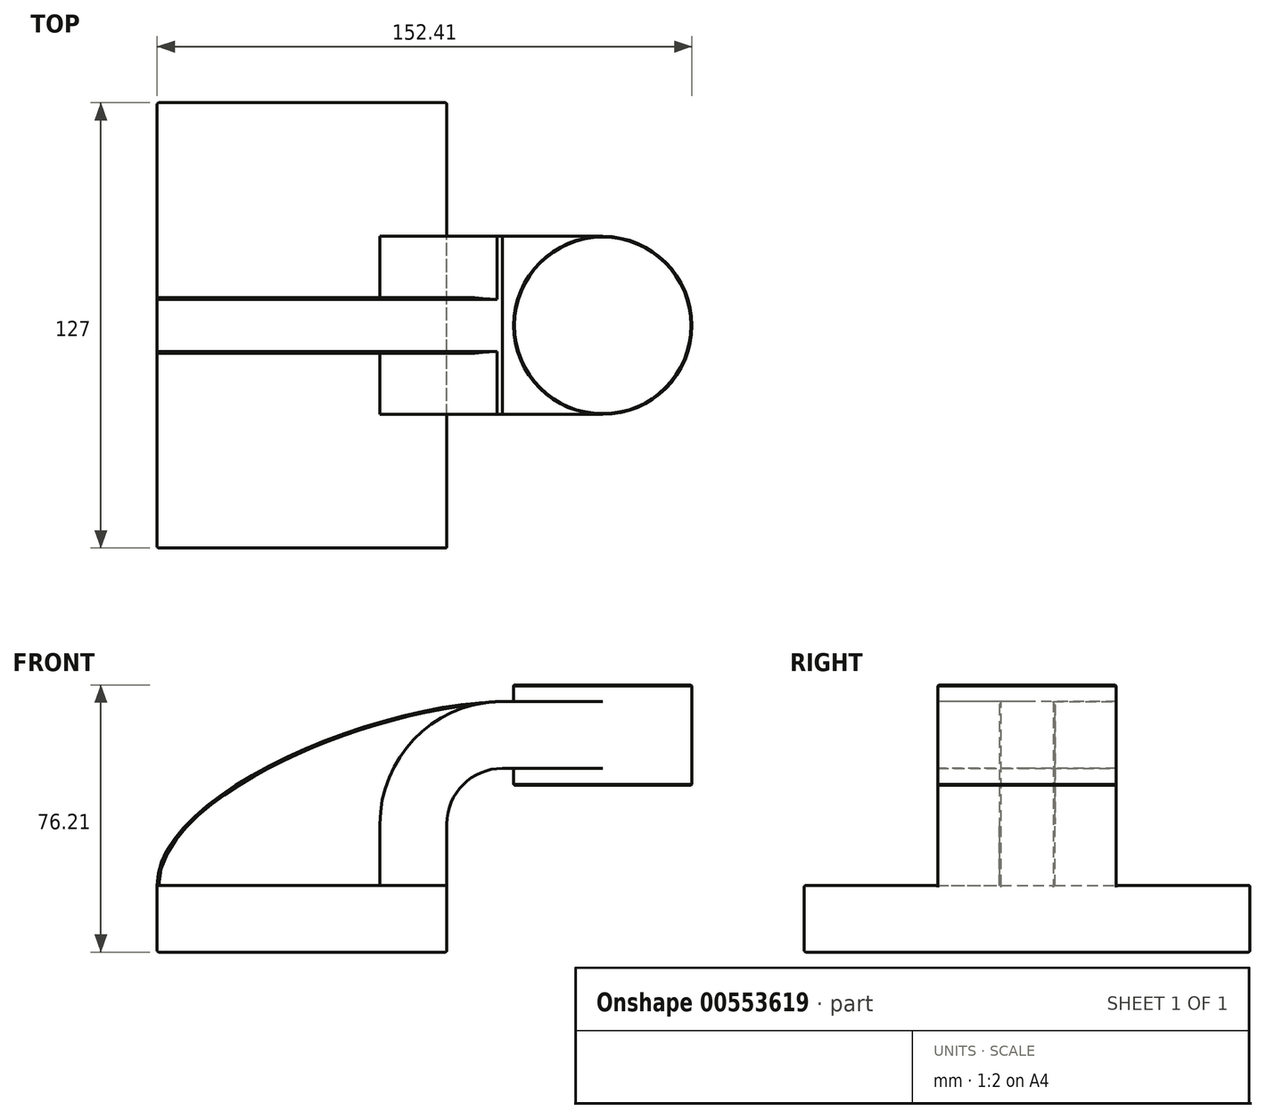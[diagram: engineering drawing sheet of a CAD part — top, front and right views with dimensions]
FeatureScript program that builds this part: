
annotation { "Feature Type Name" : "Feature", "Feature Type Description" : "" }
export const myFeature = defineFeature(function(context is Context, id is Id, definition is map)
    precondition{}
    {
        {
            var Q0;
            Q0=qCreatedBy(makeId("Front.planeOp"),FACE);
            var sketch = newSketch(context, id + "F0", { "sketchPlane" : qUnion([Q0])});
            skLineSegment(sketch, "E0.bottom", {"start": v(-41.27, -9.53) * mm, "end": v(41.28, -9.53) * mm});
            skLineSegment(sketch, "E0.top", {"start": v(-41.28, 9.52) * mm, "end": v(41.28, 9.52) * mm});
            skLineSegment(sketch, "E0.left", {"start": v(-41.28, -9.53) * mm, "end": v(-41.28, 9.52) * mm});
            skLineSegment(sketch, "E0.right", {"start": v(41.28, -9.53) * mm, "end": v(41.28, 9.52) * mm});
            skPoint(sketch, "E0.middle", {"position": v(0, 0) * mm});
            skLineSegment(sketch, "E1.bottom", {"start": v(60.33, 38.1) * mm, "end": v(111.13, 38.1) * mm});
            skLineSegment(sketch, "E1.top", {"start": v(60.33, 66.67) * mm, "end": v(111.13, 66.67) * mm});
            skLineSegment(sketch, "E1.left", {"start": v(60.33, 38.1) * mm, "end": v(60.32, 66.67) * mm});
            skLineSegment(sketch, "E1.right", {"start": v(111.13, 38.1) * mm, "end": v(111.13, 66.67) * mm});
            skPoint(sketch, "E1.middle", {"position": v(85.73, 52.39) * mm});
            skLineSegment(sketch, "E2", {"start": v(41.27, 9.52) * mm, "end": v(41.27, 27) * mm});
            skArc(sketch, "E3", {"start": v(41.27, 27) * mm, "mid": v(45.92, 38.23) * mm, "end": v(57.15, 42.88) * mm});
            skLineSegment(sketch, "E4", {"start": v(57.15, 42.88) * mm, "end": v(85.73, 42.88) * mm});
            skLineSegment(sketch, "E5.0", {"start": v(57.15, 61.93) * mm, "end": v(85.73, 61.93) * mm});
            skArc(sketch, "E5.1", {"start": v(22.22, 27) * mm, "mid": v(32.45, 51.7) * mm, "end": v(57.15, 61.93) * mm});
            skLineSegment(sketch, "E5.2", {"start": v(22.22, 9.52) * mm, "end": v(22.22, 27) * mm});
            skLineSegment(sketch, "E6", {"start": v(85.73, 38.1) * mm, "end": v(85.73, 66.67) * mm});
            skFitSpline(sketch, "E7", {"points": [v(-41.27, 9.53) * mm, v(57.15, 61.93) * mm], "startDerivative": vector(-0.82, 77.51) * mm, "endDerivative": vector(110.99, 1.46) * mm});
            skSolve(sketch);
        }
        {
            var Q0;
            Q0=makeQuery(id+"F0.imprint","IMPRINT",FACE,{"disambiguationData":[TD([[makeQuery(id+"F0.imprint","IMPRINT",EDGE,{"derivedFrom":sQuery(id+"F0.wireOp",EDGE,"E0.bottom")}),1.0]])]});
            extrude(context, id + "F1", {"entities" : qUnion([Q0]), "endBound" : BoundingType.SYMMETRIC, "depth" : 127 * mm, "offsetDistance" : 25.4 * mm});
        }
        {
            var Q0;
            {var subQ1=sQuery(id+"F0.wireOp",EDGE,"E2");Q0=makeQuery(id+"F0.imprint","IMPRINT",FACE,{"disambiguationData":[TD([[makeQuery(id+"F0.imprint","IMPRINT",EDGE,{"derivedFrom":subQ1}),1.0]])]});}
            var Q1;
            {var subQ0=sQuery(id+"F0.wireOp",EDGE,"E4");var subQ1=sQuery(id+"F0.wireOp",EDGE,"E1.left");var subQ2=makeQuery(id+"F0.imprint","INTERSECT",VERTEX,{"derivedFrom":[subQ1,subQ0]});Q1=makeQuery(id+"F0.imprint","IMPRINT",FACE,{"disambiguationData":[TD([[makeQuery(id+"F0.imprint","IMPRINT",EDGE,{"disambiguationData":[TD([[subQ2,-1.0]])],"derivedFrom":subQ1}),-1.0]])]});}
            extrude(context, id + "F2", {"entities" : qUnion([Q0, Q1]), "operationType" : NewBodyOperationType.ADD, "endBound" : BoundingType.SYMMETRIC, "depth" : 50.8 * mm, "offsetDistance" : 25.4 * mm});
        }
        {
            var Q0;
            {var subQ3=sQuery(id+"F0.wireOp",EDGE,"E5.2");Q0=makeQuery(id+"F0.imprint","IMPRINT",FACE,{"disambiguationData":[TD([[makeQuery(id+"F0.imprint","IMPRINT",EDGE,{"derivedFrom":subQ3}),1.0]])]});}
            extrude(context, id + "F3", {"entities" : qUnion([Q0]), "operationType" : NewBodyOperationType.ADD, "endBound" : BoundingType.SYMMETRIC, "depth" : 15.88 * mm, "offsetDistance" : 25.4 * mm});
        }
        {
            var Q0;
            {var subQ4=sQuery(id+"F0.wireOp",EDGE,"E1.right");Q0=makeQuery(id+"F0.imprint","IMPRINT",FACE,{"disambiguationData":[TD([[makeQuery(id+"F0.imprint","IMPRINT",EDGE,{"derivedFrom":subQ4}),1.0]])]});}
            var Q1;
            Q1=sQuery(id+"F0.wireOp",EDGE,"E6");
            revolve(context, id + "F4", {"operationType" : NewBodyOperationType.ADD, "entities" : qUnion([Q0]), "axis" : qUnion([Q1]), "revolveType" : RevolveType.FULL});
        }
        {
            var Q0;
            Q0=makeQuery(id+"F1.opExtrude","CAP_EDGE",EDGE,{"disambiguationData":[OSD([sQuery(id+"F0.wireOp",EDGE,"E0.left")])],"isStart":false});
            var Q1;
            Q1=makeQuery(id+"F1.opExtrude","CAP_EDGE",EDGE,{"disambiguationData":[OSD([sQuery(id+"F0.wireOp",EDGE,"E0.right")])],"isStart":false});
            var Q2;
            Q2=makeQuery(id+"F1.opExtrude","CAP_EDGE",EDGE,{"disambiguationData":[OSD([sQuery(id+"F0.wireOp",EDGE,"E0.top")])],"isStart":false});
            var Q3;
            {var subQ0=sQuery(id+"F0.wireOp",EDGE,"E7");var subQ1=sQuery(id+"F0.wireOp",EDGE,"E0.top");var subQ2=sQuery(id+"F0.wireOp",EDGE,"E0.left");Q3=makeQuery(id+"F3.boolean.opBoolean","SPLIT",EDGE,{"disambiguationData":[TD([makeQuery(id+"F1.opExtrude","CAP_FACE",FACE,{"disambiguationData":[OSD([sQuery(id+"F0.wireOp",EDGE,"E0.bottom"),subQ1,subQ2,sQuery(id+"F0.wireOp",EDGE,"E0.right")])],"isStart":false})])],"derivedFrom":makeQuery(id+"F1.opExtrude","SWEPT_EDGE",EDGE,{"disambiguationData":[OSD([subQ1,subQ2,subQ0])]})});}
            var Q4;
            {var subQ0=sQuery(id+"F0.wireOp",EDGE,"E0.left");var subQ1=sQuery(id+"F0.wireOp",EDGE,"E0.top");var subQ2=sQuery(id+"F0.wireOp",EDGE,"E7");Q4=makeQuery(id+"F3.boolean.opBoolean","SPLIT",EDGE,{"disambiguationData":[TD([makeQuery(id+"F1.opExtrude","CAP_FACE",FACE,{"disambiguationData":[OSD([sQuery(id+"F0.wireOp",EDGE,"E0.bottom"),subQ1,subQ0,sQuery(id+"F0.wireOp",EDGE,"E0.right")])],"isStart":true})])],"derivedFrom":makeQuery(id+"F1.opExtrude","SWEPT_EDGE",EDGE,{"disambiguationData":[OSD([subQ1,subQ0,subQ2])]})});}
            var Q5;
            Q5=makeQuery(id+"F1.opExtrude","CAP_EDGE",EDGE,{"disambiguationData":[OSD([sQuery(id+"F0.wireOp",EDGE,"E0.top")])],"isStart":true});
            var Q6;
            {var subQ0=sQuery(id+"F0.wireOp",EDGE,"E2");var subQ1=sQuery(id+"F0.wireOp",EDGE,"E0.top");var subQ2=sQuery(id+"F0.wireOp",EDGE,"E0.right");Q6=makeQuery(id+"F2.boolean.opBoolean","SPLIT",EDGE,{"disambiguationData":[TD([makeQuery(id+"F1.opExtrude","CAP_FACE",FACE,{"disambiguationData":[OSD([sQuery(id+"F0.wireOp",EDGE,"E0.bottom"),subQ1,sQuery(id+"F0.wireOp",EDGE,"E0.left"),subQ2])],"isStart":true})])],"derivedFrom":makeQuery(id+"F1.opExtrude","SWEPT_EDGE",EDGE,{"disambiguationData":[OSD([subQ1,subQ2,subQ0])]})});}
            var Q7;
            {var subQ0=sQuery(id+"F0.wireOp",EDGE,"E0.right");var subQ1=sQuery(id+"F0.wireOp",EDGE,"E2");var subQ2=sQuery(id+"F0.wireOp",EDGE,"E0.top");Q7=makeQuery(id+"F2.boolean.opBoolean","SPLIT",EDGE,{"disambiguationData":[TD([makeQuery(id+"F1.opExtrude","CAP_FACE",FACE,{"disambiguationData":[OSD([sQuery(id+"F0.wireOp",EDGE,"E0.bottom"),subQ2,sQuery(id+"F0.wireOp",EDGE,"E0.left"),subQ0])],"isStart":false})])],"derivedFrom":makeQuery(id+"F1.opExtrude","SWEPT_EDGE",EDGE,{"disambiguationData":[OSD([subQ2,subQ0,subQ1])]})});}
            var Q8;
            Q8=makeQuery(id+"F1.opExtrude","CAP_EDGE",EDGE,{"disambiguationData":[OSD([sQuery(id+"F0.wireOp",EDGE,"E0.right")])],"isStart":true});
            var Q9;
            Q9=makeQuery(id+"F1.opExtrude","CAP_EDGE",EDGE,{"disambiguationData":[OSD([sQuery(id+"F0.wireOp",EDGE,"E0.left")])],"isStart":true});
            fillet(context, id + "F5", {"entities" : qUnion([Q0, Q1, Q2, Q3, Q4, Q5, Q6, Q7, Q8, Q9]), "radius" : 0.5 * mm, "tangentPropagation" : true, "allowEdgeOverflow" : false});
        }
        {
            var Q0;
            Q0=makeQuery(id+"F3.opExtrude","CAP_EDGE",EDGE,{"disambiguationData":[OSD([sQuery(id+"F0.wireOp",EDGE,"E7")])],"isStart":false});
            var Q1;
            Q1=makeQuery(id+"F3.opExtrude","CAP_EDGE",EDGE,{"disambiguationData":[OSD([sQuery(id+"F0.wireOp",EDGE,"E7")])],"isStart":true});
            chamfer(context, id + "F6", {"entities" : qUnion([Q0, Q1]), "width" : 0.5 * mm, "tangentPropagation" : true});
        }
        {
            var Q0;
            Q0=makeQuery(id+"F4.opRevolve","SWEPT_EDGE",EDGE,{"disambiguationData":[OSD([sQuery(id+"F0.wireOp",EDGE,"E1.top"),sQuery(id+"F0.wireOp",EDGE,"E1.right")])]});
            var Q1;
            Q1=makeQuery(id+"F4.opRevolve","SWEPT_EDGE",EDGE,{"disambiguationData":[OSD([sQuery(id+"F0.wireOp",EDGE,"E1.bottom"),sQuery(id+"F0.wireOp",EDGE,"E1.right")])]});
            chamfer(context, id + "F7", {"entities" : qUnion([Q0, Q1]), "width" : 0.25 * mm, "tangentPropagation" : true});
        }
        {
            var Q0;
            Q0=makeQuery(id+"F1.opExtrude","SWEPT_EDGE",EDGE,{"disambiguationData":[OSD([sQuery(id+"F0.wireOp",EDGE,"E0.bottom"),sQuery(id+"F0.wireOp",EDGE,"E0.left")])]});
            var Q1;
            Q1=makeQuery(id+"F1.opExtrude","CAP_EDGE",EDGE,{"disambiguationData":[OSD([sQuery(id+"F0.wireOp",EDGE,"E0.bottom")])],"isStart":true});
            var Q2;
            Q2=makeQuery(id+"F1.opExtrude","SWEPT_EDGE",EDGE,{"disambiguationData":[OSD([sQuery(id+"F0.wireOp",EDGE,"E0.bottom"),sQuery(id+"F0.wireOp",EDGE,"E0.right")])]});
            var Q3;
            Q3=makeQuery(id+"F1.opExtrude","CAP_EDGE",EDGE,{"disambiguationData":[OSD([sQuery(id+"F0.wireOp",EDGE,"E0.bottom")])],"isStart":false});
            fillet(context, id + "F8", {"entities" : qUnion([Q0, Q1, Q2, Q3]), "radius" : 0.5 * mm, "tangentPropagation" : true, "allowEdgeOverflow" : false});
        }
    });
